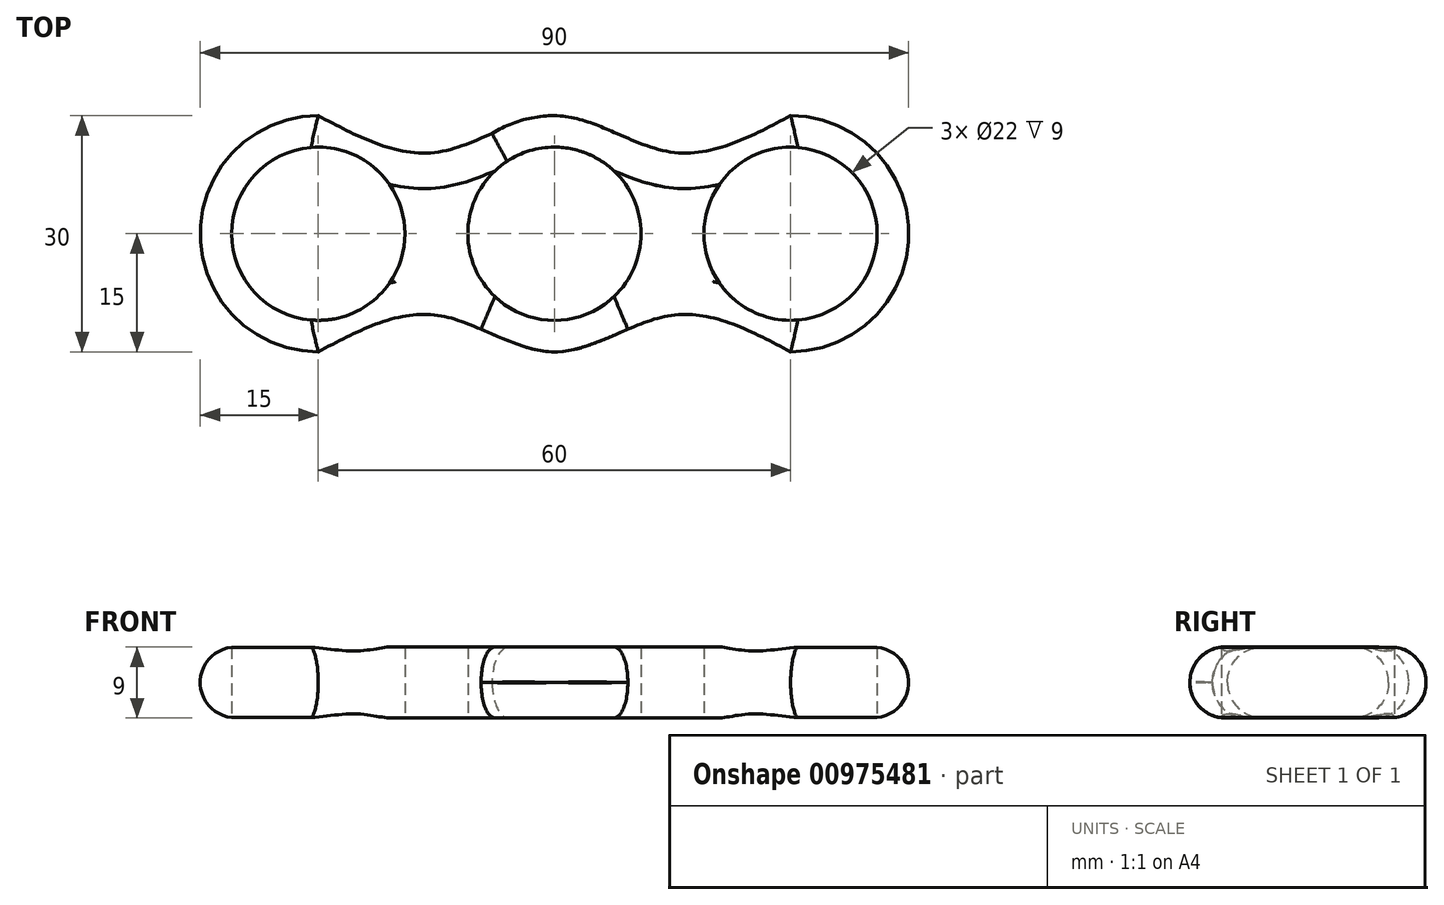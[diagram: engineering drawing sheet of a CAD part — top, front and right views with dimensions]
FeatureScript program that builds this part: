
annotation { "Feature Type Name" : "Feature", "Feature Type Description" : "" }
export const myFeature = defineFeature(function(context is Context, id is Id, definition is map)
    precondition{}
    {
        {
            var Q0;
            Q0=qCreatedBy(makeId("Top.planeOp"),FACE);
            var sketch = newSketch(context, id + "F0", { "sketchPlane" : qUnion([Q0])});
            skCircle(sketch, "E0", {"center": v(0, 0) * mm, "radius": 11 * mm});
            skCircle(sketch, "E1", {"center": v(30, 0) * mm, "radius": 11 * mm});
            skCircle(sketch, "E2", {"center": v(-30, 0) * mm, "radius": 11 * mm});
            skArc(sketch, "E3.0", {"start": v(-30, -15) * mm, "mid": v(-15, 0) * mm, "end": v(-30, 15) * mm});
            skArc(sketch, "E4.0", {"start": v(7.92, -12.74) * mm, "mid": v(15, 0) * mm, "end": v(7.92, 12.74) * mm});
            skArc(sketch, "E5.0", {"start": v(30, -15) * mm, "mid": v(45, 0) * mm, "end": v(30, 15) * mm});
            skPoint(sketch, "E6", {"position": v(30, 15) * mm});
            skPoint(sketch, "E7", {"position": v(0, 15) * mm});
            skPoint(sketch, "E8", {"position": v(-30, 15) * mm});
            skPoint(sketch, "E9", {"position": v(-30, -15) * mm});
            skPoint(sketch, "E10", {"position": v(0, -15) * mm});
            skPoint(sketch, "E11", {"position": v(30, -15) * mm});
            skPoint(sketch, "E12", {"position": v(15, 0) * mm});
            skPoint(sketch, "E13", {"position": v(-15, 0) * mm});
            skLineSegment(sketch, "E14", {"start": v(15, 0) * mm, "end": v(-15, 0) * mm});
            skPoint(sketch, "E15", {"position": v(15, -10.34) * mm});
            skPoint(sketch, "E16", {"position": v(-15, -10.34) * mm});
            skFitSpline(sketch, "E17", {"points": [v(30, -15) * mm, v(15, -10.34) * mm, v(0, -15) * mm, v(-15, -10.34) * mm, v(-30, -15) * mm], "startDerivative": vector(-60, 31.93) * mm, "endDerivative": vector(-60, -31.93) * mm});
            skFitSpline(sketch, "E18.MirrorCS", {"points": [v(30, 15) * mm, v(15, 10.34) * mm, v(0, 15) * mm, v(-15, 10.34) * mm, v(-30, 15) * mm], "startDerivative": vector(-60, -31.93) * mm, "endDerivative": vector(-60, 31.93) * mm});
            skArc(sketch, "E19.trimOffspring", {"start": v(30, 15) * mm, "mid": v(15, 0) * mm, "end": v(30, -15) * mm});
            skArc(sketch, "E20.trimOffspring", {"start": v(0, 15) * mm, "mid": v(-14.42, 4.12) * mm, "end": v(-7.92, -12.74) * mm});
            skArc(sketch, "E21.trimOffspring", {"start": v(-30, 15) * mm, "mid": v(-45, 0) * mm, "end": v(-30, -15) * mm});
            skSolve(sketch);
        }
        {
            var Q0;
            {var subQ0=sQuery(id+"F0.wireOp",EDGE,"E20.trimOffspring");var subQ1=sQuery(id+"F0.wireOp",EDGE,"E18.MirrorCS");var subQ2=makeQuery(id+"F0.imprint","INTERSECT",VERTEX,{"disambiguationData":[OD(0.0)],"derivedFrom":[subQ1,subQ0]});Q0=makeQuery(id+"F0.imprint","IMPRINT",FACE,{"disambiguationData":[TD([[makeQuery(id+"F0.imprint","IMPRINT",EDGE,{"disambiguationData":[TD([[subQ2,-1.0]])],"derivedFrom":subQ1}),-1.0]])]});}
            var Q1;
            {var subQ0=sQuery(id+"F0.wireOp",EDGE,"E20.trimOffspring");var subQ3=sQuery(id+"F0.wireOp",EDGE,"E17");var subQ5=makeQuery(id+"F0.imprint","INTERSECT",VERTEX,{"derivedFrom":[subQ3,subQ0]});Q1=makeQuery(id+"F0.imprint","IMPRINT",FACE,{"disambiguationData":[TD([[makeQuery(id+"F0.imprint","IMPRINT",EDGE,{"disambiguationData":[TD([[subQ5,-1.0]])],"derivedFrom":subQ3}),-1.0]])]});}
            var Q2;
            {var subQ1=sQuery(id+"F0.wireOp",EDGE,"E3.0");var subQ3=sQuery(id+"F0.wireOp",EDGE,"E18.MirrorCS");var subQ4=makeQuery(id+"F0.imprint","INTERSECT",VERTEX,{"derivedFrom":[subQ1,subQ3]});Q2=makeQuery(id+"F0.imprint","IMPRINT",FACE,{"disambiguationData":[TD([[makeQuery(id+"F0.imprint","IMPRINT",EDGE,{"disambiguationData":[TD([[subQ4,1.0]])],"derivedFrom":subQ3}),1.0]])]});}
            var Q3;
            {var subQ0=sQuery(id+"F0.wireOp",EDGE,"E17");var subQ1=sQuery(id+"F0.wireOp",EDGE,"E4.0");var subQ2=makeQuery(id+"F0.imprint","INTERSECT",VERTEX,{"derivedFrom":[subQ1,subQ0]});Q3=makeQuery(id+"F0.imprint","IMPRINT",FACE,{"disambiguationData":[TD([[makeQuery(id+"F0.imprint","IMPRINT",EDGE,{"disambiguationData":[TD([[subQ2,1.0]])],"derivedFrom":subQ0}),-1.0]])]});}
            var Q4;
            {var subQ0=sQuery(id+"F0.wireOp",EDGE,"E18.MirrorCS");var subQ1=sQuery(id+"F0.wireOp",EDGE,"E4.0");var subQ2=makeQuery(id+"F0.imprint","INTERSECT",VERTEX,{"derivedFrom":[subQ1,subQ0]});Q4=makeQuery(id+"F0.imprint","IMPRINT",FACE,{"disambiguationData":[TD([[makeQuery(id+"F0.imprint","IMPRINT",EDGE,{"disambiguationData":[TD([[subQ2,1.0]])],"derivedFrom":subQ0}),1.0]])]});}
            var Q5;
            {var subQ1=sQuery(id+"F0.wireOp",EDGE,"E14");var subQ3=sQuery(id+"F0.wireOp",EDGE,"E0");var subQ9=makeQuery(id+"F0.imprint","INTERSECT",VERTEX,{"disambiguationData":[OD(0.0)],"derivedFrom":[subQ3,subQ1]});Q5=makeQuery(id+"F0.imprint","IMPRINT",FACE,{"disambiguationData":[TD([[makeQuery(id+"F0.imprint","IMPRINT",EDGE,{"disambiguationData":[TD([[subQ9,1.0]])],"derivedFrom":subQ3}),-1.0]])]});}
            var Q6;
            {var subQ1=sQuery(id+"F0.wireOp",EDGE,"E14");var subQ3=sQuery(id+"F0.wireOp",EDGE,"E0");var subQ7=makeQuery(id+"F0.imprint","INTERSECT",VERTEX,{"disambiguationData":[OD(0.0)],"derivedFrom":[subQ3,subQ1]});Q6=makeQuery(id+"F0.imprint","IMPRINT",FACE,{"disambiguationData":[TD([[makeQuery(id+"F0.imprint","IMPRINT",EDGE,{"disambiguationData":[TD([[subQ7,-1.0]])],"derivedFrom":subQ3}),-1.0]])]});}
            var Q7;
            Q7=makeQuery(id+"F0.imprint","IMPRINT",FACE,{"disambiguationData":[TD([[makeQuery(id+"F0.imprint","IMPRINT",EDGE,{"derivedFrom":sQuery(id+"F0.wireOp",EDGE,"E1")}),-1.0]])]});
            var Q8;
            Q8=makeQuery(id+"F0.imprint","IMPRINT",FACE,{"disambiguationData":[TD([[makeQuery(id+"F0.imprint","IMPRINT",EDGE,{"derivedFrom":sQuery(id+"F0.wireOp",EDGE,"E2")}),-1.0]])]});
            extrude(context, id + "F1", {"entities" : qUnion([Q0, Q1, Q2, Q3, Q4, Q5, Q6, Q7, Q8]), "depth" : 9 * mm, "offsetDistance" : 25.4 * mm});
        }
        {
            var Q0;
            Q0=makeQuery(id+"F1.opExtrude","CAP_EDGE",EDGE,{"disambiguationData":[OSD([sQuery(id+"F0.wireOp",EDGE,"E17")])],"isStart":false});
            var Q1;
            Q1=makeQuery(id+"F1.opExtrude","CAP_EDGE",EDGE,{"disambiguationData":[OSD([sQuery(id+"F0.wireOp",EDGE,"E20.trimOffspring")])],"isStart":false});
            var Q2;
            {var subQ0=sQuery(id+"F0.wireOp",EDGE,"E18.MirrorCS");var subQ1=sQuery(id+"F0.wireOp",EDGE,"E3.0");var subQ2=makeQuery(id+"F0.imprint","INTERSECT",VERTEX,{"derivedFrom":[subQ1,subQ0]});Q2=makeQuery(id+"F1.opExtrude","CAP_EDGE",EDGE,{"disambiguationData":[OSD([subQ0]),TDD([makeQuery(id+"F0.imprint","IMPRINT",EDGE,{"disambiguationData":[TD([[subQ2,1.0]])],"derivedFrom":subQ0}),makeQuery(id+"F0.imprint","IMPRINT",EDGE,{"disambiguationData":[TD([[subQ2,-1.0]])],"derivedFrom":subQ0})])],"isStart":false});}
            var Q3;
            Q3=makeQuery(id+"F1.opExtrude","CAP_EDGE",EDGE,{"disambiguationData":[OSD([sQuery(id+"F0.wireOp",EDGE,"E17")])],"isStart":true});
            var Q4;
            {var subQ0=sQuery(id+"F0.wireOp",EDGE,"E18.MirrorCS");var subQ1=makeQuery(id+"F0.imprint","INTERSECT",VERTEX,{"derivedFrom":[sQuery(id+"F0.wireOp",EDGE,"E4.0"),subQ0]});var subQ2=sQuery(id+"F0.wireOp",EDGE,"E19.trimOffspring");var subQ3=makeQuery(id+"F0.imprint","INTERSECT",VERTEX,{"derivedFrom":[subQ0,subQ2]});Q4=makeQuery(id+"F1.opExtrude","CAP_EDGE",EDGE,{"disambiguationData":[OSD([subQ0]),TDD([makeQuery(id+"F0.imprint","IMPRINT",EDGE,{"disambiguationData":[TD([[subQ3,1.0]])],"derivedFrom":subQ0}),makeQuery(id+"F0.imprint","IMPRINT",EDGE,{"disambiguationData":[TD([[subQ1,1.0]])],"derivedFrom":subQ0}),makeQuery(id+"F0.imprint","IMPRINT",EDGE,{"disambiguationData":[TD([[subQ1,-1.0]])],"derivedFrom":subQ0})])],"isStart":true});}
            var Q5;
            {var subQ0=sQuery(id+"F0.wireOp",EDGE,"E18.MirrorCS");var subQ1=sQuery(id+"F0.wireOp",EDGE,"E3.0");var subQ2=makeQuery(id+"F0.imprint","INTERSECT",VERTEX,{"derivedFrom":[subQ1,subQ0]});Q5=makeQuery(id+"F1.opExtrude","CAP_EDGE",EDGE,{"disambiguationData":[OSD([subQ0]),TDD([makeQuery(id+"F0.imprint","IMPRINT",EDGE,{"disambiguationData":[TD([[subQ2,1.0]])],"derivedFrom":subQ0}),makeQuery(id+"F0.imprint","IMPRINT",EDGE,{"disambiguationData":[TD([[subQ2,-1.0]])],"derivedFrom":subQ0})])],"isStart":true});}
            var Q6;
            Q6=makeQuery(id+"F1.opExtrude","CAP_EDGE",EDGE,{"disambiguationData":[OSD([sQuery(id+"F0.wireOp",EDGE,"E21.trimOffspring")])],"isStart":false});
            var Q7;
            Q7=makeQuery(id+"F1.opExtrude","CAP_EDGE",EDGE,{"disambiguationData":[OSD([sQuery(id+"F0.wireOp",EDGE,"E21.trimOffspring")])],"isStart":true});
            var Q8;
            Q8=makeQuery(id+"F1.opExtrude","CAP_EDGE",EDGE,{"disambiguationData":[OSD([sQuery(id+"F0.wireOp",EDGE,"E5.0")])],"isStart":false});
            var Q9;
            Q9=makeQuery(id+"F1.opExtrude","CAP_EDGE",EDGE,{"disambiguationData":[OSD([sQuery(id+"F0.wireOp",EDGE,"E5.0")])],"isStart":true});
            fillet(context, id + "F2", {"entities" : qUnion([Q0, Q1, Q2, Q3, Q4, Q5, Q6, Q7, Q8, Q9]), "radius" : 4.5 * mm, "tangentPropagation" : true, "allowEdgeOverflow" : false});
        }
    });
